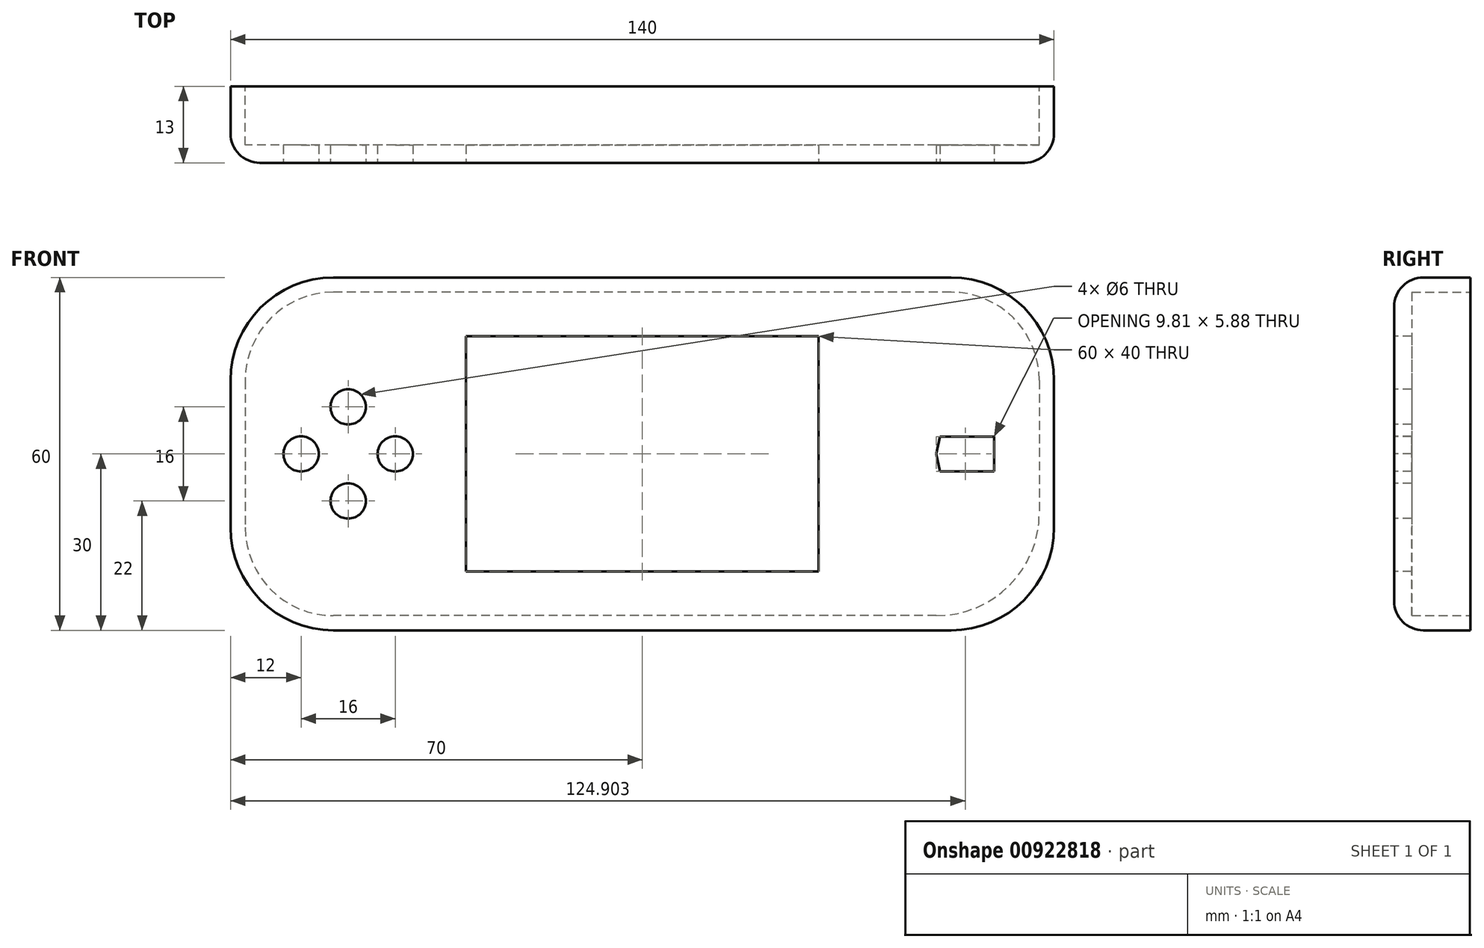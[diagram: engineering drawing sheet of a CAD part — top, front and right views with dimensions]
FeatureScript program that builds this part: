
annotation { "Feature Type Name" : "Feature", "Feature Type Description" : "" }
export const myFeature = defineFeature(function(context is Context, id is Id, definition is map)
    precondition{}
    {
        {
            var Q0;
            Q0=qCreatedBy(makeId("Front.planeOp"),FACE);
            var sketch = newSketch(context, id + "F0", { "sketchPlane" : qUnion([Q0])});
            skLineSegment(sketch, "E0.bottom", {"start": v(-70, 30) * mm, "end": v(70, 30) * mm});
            skLineSegment(sketch, "E0.top", {"start": v(-70, -30) * mm, "end": v(70, -30) * mm});
            skLineSegment(sketch, "E0.left", {"start": v(-70, 30) * mm, "end": v(-70, -30) * mm});
            skLineSegment(sketch, "E0.right", {"start": v(70, 30) * mm, "end": v(70, -30) * mm});
            skPoint(sketch, "E0.middle", {"position": v(0, 0) * mm});
            skSolve(sketch);
        }
        {
            var Q0;
            Q0 = qSketchRegion(id + "F0", true);
            extrude(context, id + "F1", {"entities" : qUnion([Q0]), "depth" : 13 * mm, "offsetDistance" : 25 * mm});
        }
        {
            var Q0;
            Q0=makeQuery(id+"F1.opExtrude","CAP_FACE",FACE,{"disambiguationData":[OSD([sQuery(id+"F0.wireOp",EDGE,"E0.bottom"),sQuery(id+"F0.wireOp",EDGE,"E0.top"),sQuery(id+"F0.wireOp",EDGE,"E0.left"),sQuery(id+"F0.wireOp",EDGE,"E0.right")])],"isStart":false});
            fillet(context, id + "F2", {"entities" : qUnion([Q0]), "radius" : 5 * mm, "tangentPropagation" : true, "allowEdgeOverflow" : false});
        }
        {
            var Q0;
            Q0=makeQuery(id+"F1.opExtrude","SWEPT_EDGE",EDGE,{"disambiguationData":[OSD([sQuery(id+"F0.wireOp",EDGE,"E0.bottom"),sQuery(id+"F0.wireOp",EDGE,"E0.left")])]});
            var Q1;
            Q1=makeQuery(id+"F1.opExtrude","SWEPT_EDGE",EDGE,{"disambiguationData":[OSD([sQuery(id+"F0.wireOp",EDGE,"E0.top"),sQuery(id+"F0.wireOp",EDGE,"E0.left")])]});
            var Q2;
            Q2=makeQuery(id+"F2.opFillet","BLEND_EDGE",EDGE,{"blendedFrom":[makeQuery(id+"F1.opExtrude","CAP_EDGE",EDGE,{"disambiguationData":[OSD([sQuery(id+"F0.wireOp",EDGE,"E0.bottom")])],"isStart":false}),makeQuery(id+"F1.opExtrude","CAP_EDGE",EDGE,{"disambiguationData":[OSD([sQuery(id+"F0.wireOp",EDGE,"E0.right")])],"isStart":false})],"blendedInto":[]});
            var Q3;
            Q3=makeQuery(id+"F2.opFillet","BLEND_EDGE",EDGE,{"blendedFrom":[makeQuery(id+"F1.opExtrude","CAP_EDGE",EDGE,{"disambiguationData":[OSD([sQuery(id+"F0.wireOp",EDGE,"E0.top")])],"isStart":false}),makeQuery(id+"F1.opExtrude","CAP_EDGE",EDGE,{"disambiguationData":[OSD([sQuery(id+"F0.wireOp",EDGE,"E0.right")])],"isStart":false})],"blendedInto":[]});
            fillet(context, id + "F3", {"entities" : qUnion([Q0, Q1, Q2, Q3]), "radius" : 17.5 * mm, "tangentPropagation" : true, "allowEdgeOverflow" : false});
        }
        {
            var Q0;
            Q0=makeQuery(id+"F1.opExtrude","CAP_FACE",FACE,{"disambiguationData":[OSD([sQuery(id+"F0.wireOp",EDGE,"E0.bottom"),sQuery(id+"F0.wireOp",EDGE,"E0.top"),sQuery(id+"F0.wireOp",EDGE,"E0.left"),sQuery(id+"F0.wireOp",EDGE,"E0.right")])],"isStart":false});
            var sketch = newSketch(context, id + "F4", { "sketchPlane" : qUnion([Q0])});
            skLineSegment(sketch, "E1", {"start": v(0, 0) * mm, "end": v(-50, 0) * mm});
            skLineSegment(sketch, "E2", {"start": v(0, 0) * mm, "end": v(50, 0) * mm});
            skLineSegment(sketch, "E3", {"start": v(-50, 0) * mm, "end": v(-50, 8) * mm});
            skLineSegment(sketch, "E4", {"start": v(-50, 0) * mm, "end": v(-42, 0) * mm});
            skLineSegment(sketch, "E5", {"start": v(-50, 0) * mm, "end": v(-50, -8) * mm});
            skLineSegment(sketch, "E6", {"start": v(-50, 0) * mm, "end": v(-58, 0) * mm});
            skLineSegment(sketch, "E7", {"start": v(50, 0) * mm, "end": v(52.5, 12.5) * mm});
            skLineSegment(sketch, "E8", {"start": v(52.5, 12.5) * mm, "end": v(50, 0) * mm});
            skLineSegment(sketch, "E9", {"start": v(50, 0) * mm, "end": v(52.5, -12.5) * mm});
            skLineSegment(sketch, "E10", {"start": v(52.5, -12.5) * mm, "end": v(50, 0) * mm});
            skLineSegment(sketch, "E11", {"start": v(50, 0) * mm, "end": v(59.8, 1.96) * mm});
            skLineSegment(sketch, "E12", {"start": v(50, 0) * mm, "end": v(40, 0) * mm});
            skCircle(sketch, "E13", {"center": v(-50, 8) * mm, "radius": 3 * mm});
            skCircle(sketch, "E14", {"center": v(-58, 0) * mm, "radius": 3 * mm});
            skCircle(sketch, "E15", {"center": v(-42, 0) * mm, "radius": 3 * mm});
            skCircle(sketch, "E16", {"center": v(-50, -8) * mm, "radius": 3 * mm});
            skLineSegment(sketch, "E17", {"start": v(50, 0) * mm, "end": v(47, 0) * mm});
            skLineSegment(sketch, "E18", {"start": v(50, 0) * mm, "end": v(50.59, 2.94) * mm});
            skLineSegment(sketch, "E19", {"start": v(50, 0) * mm, "end": v(52.94, 0.59) * mm});
            skLineSegment(sketch, "E20", {"start": v(50, 0) * mm, "end": v(50.59, -2.94) * mm});
            skLineSegment(sketch, "E21.bottom", {"start": v(47, 2.94) * mm, "end": v(52.94, 2.94) * mm});
            skLineSegment(sketch, "E21.top", {"start": v(47, 12.5) * mm, "end": v(52.94, 12.5) * mm});
            skLineSegment(sketch, "E21.left", {"start": v(47, 2.94) * mm, "end": v(47, 12.5) * mm});
            skLineSegment(sketch, "E21.right", {"start": v(52.94, 2.94) * mm, "end": v(52.94, 12.5) * mm});
            skLineSegment(sketch, "E22.bottom", {"start": v(47, 2.94) * mm, "end": v(40, 2.94) * mm});
            skLineSegment(sketch, "E22.top", {"start": v(47, -2.94) * mm, "end": v(40, -2.94) * mm});
            skLineSegment(sketch, "E22.left", {"start": v(47, 2.94) * mm, "end": v(47, -2.94) * mm});
            skLineSegment(sketch, "E22.right", {"start": v(40, 2.94) * mm, "end": v(40, -2.94) * mm});
            skLineSegment(sketch, "E23.bottom", {"start": v(47, -2.94) * mm, "end": v(52.94, -2.94) * mm});
            skLineSegment(sketch, "E23.top", {"start": v(47, -12.5) * mm, "end": v(52.94, -12.5) * mm});
            skLineSegment(sketch, "E23.left", {"start": v(47, -2.94) * mm, "end": v(47, -12.5) * mm});
            skLineSegment(sketch, "E23.right", {"start": v(52.94, -2.94) * mm, "end": v(52.94, -12.5) * mm});
            skLineSegment(sketch, "E24.bottom", {"start": v(52.94, -2.94) * mm, "end": v(59.8, -2.94) * mm});
            skLineSegment(sketch, "E24.top", {"start": v(52.94, 2.94) * mm, "end": v(59.8, 2.94) * mm});
            skLineSegment(sketch, "E24.left", {"start": v(52.94, -2.94) * mm, "end": v(52.94, 2.94) * mm});
            skLineSegment(sketch, "E24.right", {"start": v(59.8, -2.94) * mm, "end": v(59.8, 2.94) * mm});
            skSolve(sketch);
        }
        {
            var Q0;
            Q0=makeQuery(id+"F4.imprint","IMPRINT",FACE,{"disambiguationData":[TD([[makeQuery(id+"F4.imprint","IMPRINT",EDGE,{"derivedFrom":sQuery(id+"F4.wireOp",EDGE,"E16")}),1.0]])]});
            var Q1;
            {var subQ0=sQuery(id+"F4.wireOp",EDGE,"E4");var subQ1=sQuery(id+"F4.wireOp",EDGE,"E1");var subQ2=makeQuery(id+"F4.imprint","INTERSECT",VERTEX,{"derivedFrom":[subQ1,subQ0]});Q1=makeQuery(id+"F4.imprint","IMPRINT",FACE,{"disambiguationData":[TD([[makeQuery(id+"F4.imprint","IMPRINT",EDGE,{"disambiguationData":[TD([[subQ2,1.0]])],"derivedFrom":subQ1}),1.0]])]});}
            var Q2;
            {var subQ0=sQuery(id+"F4.wireOp",EDGE,"E4");var subQ1=sQuery(id+"F4.wireOp",EDGE,"E1");var subQ2=makeQuery(id+"F4.imprint","INTERSECT",VERTEX,{"derivedFrom":[subQ1,subQ0]});Q2=makeQuery(id+"F4.imprint","IMPRINT",FACE,{"disambiguationData":[TD([[makeQuery(id+"F4.imprint","IMPRINT",EDGE,{"disambiguationData":[TD([[subQ2,1.0]])],"derivedFrom":subQ1}),-1.0]])]});}
            var Q3;
            Q3=makeQuery(id+"F4.imprint","IMPRINT",FACE,{"disambiguationData":[TD([[makeQuery(id+"F4.imprint","IMPRINT",EDGE,{"derivedFrom":sQuery(id+"F4.wireOp",EDGE,"E14")}),1.0]])]});
            var Q4;
            Q4=makeQuery(id+"F4.imprint","IMPRINT",FACE,{"disambiguationData":[TD([[makeQuery(id+"F4.imprint","IMPRINT",EDGE,{"derivedFrom":sQuery(id+"F4.wireOp",EDGE,"E13")}),1.0]])]});
            var Q5;
            {var subQ0=sQuery(id+"F4.wireOp",EDGE,"E8");Q5=makeQuery(id+"F4.imprint","IMPRINT",FACE,{"disambiguationData":[TD([[makeQuery(id+"F4.imprint","IMPRINT",EDGE,{"derivedFrom":subQ0}),-1.0]])]});}
            var Q6;
            {var subQ0=sQuery(id+"F4.wireOp",EDGE,"E8");Q6=makeQuery(id+"F4.imprint","IMPRINT",FACE,{"disambiguationData":[TD([[makeQuery(id+"F4.imprint","IMPRINT",EDGE,{"derivedFrom":subQ0}),1.0]])]});}
            var Q7;
            {var subQ0=sQuery(id+"F4.wireOp",EDGE,"E18");Q7=makeQuery(id+"F4.imprint","IMPRINT",FACE,{"disambiguationData":[TD([[makeQuery(id+"F4.imprint","IMPRINT",EDGE,{"derivedFrom":subQ0}),-1.0]])]});}
            var Q8;
            {var subQ0=sQuery(id+"F4.wireOp",EDGE,"E17");Q8=makeQuery(id+"F4.imprint","IMPRINT",FACE,{"disambiguationData":[TD([[makeQuery(id+"F4.imprint","IMPRINT",EDGE,{"derivedFrom":subQ0}),-1.0]])]});}
            var Q9;
            {var subQ0=sQuery(id+"F4.wireOp",EDGE,"E17");Q9=makeQuery(id+"F4.imprint","IMPRINT",FACE,{"disambiguationData":[TD([[makeQuery(id+"F4.imprint","IMPRINT",EDGE,{"derivedFrom":subQ0}),1.0]])]});}
            var Q10;
            {var subQ0=sQuery(id+"F4.wireOp",EDGE,"E19");Q10=makeQuery(id+"F4.imprint","IMPRINT",FACE,{"disambiguationData":[TD([[makeQuery(id+"F4.imprint","IMPRINT",EDGE,{"derivedFrom":subQ0}),-1.0]])]});}
            var Q11;
            {var subQ0=sQuery(id+"F4.wireOp",EDGE,"E11");Q11=makeQuery(id+"F4.imprint","IMPRINT",FACE,{"disambiguationData":[TD([[makeQuery(id+"F4.imprint","IMPRINT",EDGE,{"derivedFrom":subQ0}),1.0]])]});}
            var Q12;
            {var subQ0=sQuery(id+"F4.wireOp",EDGE,"E11");Q12=makeQuery(id+"F4.imprint","IMPRINT",FACE,{"disambiguationData":[TD([[makeQuery(id+"F4.imprint","IMPRINT",EDGE,{"derivedFrom":subQ0}),-1.0]])]});}
            var Q13;
            {var subQ0=sQuery(id+"F4.wireOp",EDGE,"E12");Q13=makeQuery(id+"F4.imprint","IMPRINT",FACE,{"disambiguationData":[TD([[makeQuery(id+"F4.imprint","IMPRINT",EDGE,{"derivedFrom":subQ0}),-1.0]])]});}
            var Q14;
            {var subQ0=sQuery(id+"F4.wireOp",EDGE,"E12");Q14=makeQuery(id+"F4.imprint","IMPRINT",FACE,{"disambiguationData":[TD([[makeQuery(id+"F4.imprint","IMPRINT",EDGE,{"derivedFrom":subQ0}),1.0]])]});}
            var Q15;
            {var subQ0=sQuery(id+"F4.wireOp",EDGE,"E10");Q15=makeQuery(id+"F4.imprint","IMPRINT",FACE,{"disambiguationData":[TD([[makeQuery(id+"F4.imprint","IMPRINT",EDGE,{"derivedFrom":subQ0}),1.0]])]});}
            var Q16;
            {var subQ0=sQuery(id+"F4.wireOp",EDGE,"E10");Q16=makeQuery(id+"F4.imprint","IMPRINT",FACE,{"disambiguationData":[TD([[makeQuery(id+"F4.imprint","IMPRINT",EDGE,{"derivedFrom":subQ0}),-1.0]])]});}
            extrude(context, id + "F5", {"entities" : qUnion([Q0, Q1, Q2, Q3, Q4, Q5, Q6, Q7, Q8, Q9, Q10, Q11, Q12, Q13, Q14, Q15, Q16]), "operationType" : NewBodyOperationType.REMOVE, "oppositeDirection" : true, "depth" : 25 * mm, "offsetDistance" : 25 * mm});
        }
        {
            var Q0;
            Q0=makeQuery(id+"F1.opExtrude","CAP_FACE",FACE,{"disambiguationData":[OSD([sQuery(id+"F0.wireOp",EDGE,"E0.bottom"),sQuery(id+"F0.wireOp",EDGE,"E0.top"),sQuery(id+"F0.wireOp",EDGE,"E0.left"),sQuery(id+"F0.wireOp",EDGE,"E0.right")])],"isStart":false});
            var sketch = newSketch(context, id + "F6", { "sketchPlane" : qUnion([Q0])});
            skLineSegment(sketch, "E25.bottom", {"start": v(-30, 20) * mm, "end": v(30, 20) * mm});
            skLineSegment(sketch, "E25.top", {"start": v(-30, -20) * mm, "end": v(30, -20) * mm});
            skLineSegment(sketch, "E25.left", {"start": v(-30, 20) * mm, "end": v(-30, -20) * mm});
            skLineSegment(sketch, "E25.right", {"start": v(30, 20) * mm, "end": v(30, -20) * mm});
            skPoint(sketch, "E25.middle", {"position": v(0, 0) * mm});
            skSolve(sketch);
        }
        {
            var Q0;
            Q0=makeQuery(id+"F6.imprint","IMPRINT",FACE,{"disambiguationData":[TD([[makeQuery(id+"F6.imprint","IMPRINT",EDGE,{"derivedFrom":sQuery(id+"F6.wireOp",EDGE,"E25.bottom")}),-1.0]])]});
            extrude(context, id + "F7", {"entities" : qUnion([Q0]), "operationType" : NewBodyOperationType.REMOVE, "oppositeDirection" : true, "depth" : 25 * mm, "offsetDistance" : 25 * mm});
        }
        {
            var Q0;
            Q0=makeQuery(id+"F1.opExtrude","CAP_FACE",FACE,{"disambiguationData":[OSD([sQuery(id+"F0.wireOp",EDGE,"E0.bottom"),sQuery(id+"F0.wireOp",EDGE,"E0.top"),sQuery(id+"F0.wireOp",EDGE,"E0.left"),sQuery(id+"F0.wireOp",EDGE,"E0.right")])],"isStart":true});
            var sketch = newSketch(context, id + "F8", { "sketchPlane" : qUnion([Q0])});
            skLineSegment(sketch, "E26.bottom", {"start": v(-52.5, 27.5) * mm, "end": v(52.5, 27.5) * mm});
            skLineSegment(sketch, "E26.top", {"start": v(-50, -27.5) * mm, "end": v(52.5, -27.5) * mm});
            skLineSegment(sketch, "E26.left", {"start": v(-67.5, 12.5) * mm, "end": v(-67.5, -10) * mm});
            skLineSegment(sketch, "E26.right", {"start": v(67.5, 12.5) * mm, "end": v(67.5, -12.5) * mm});
            skPoint(sketch, "E26.middle", {"position": v(0, 0) * mm});
            skPoint(sketch, "E27.visualSharp", {"position": v(-67.5, -27.5) * mm});
            skArc(sketch, "E27.filletArc", {"start": v(-67.5, -10) * mm, "mid": v(-62.37, -22.37) * mm, "end": v(-50, -27.5) * mm});
            skPoint(sketch, "E28.visualSharp", {"position": v(-67.5, 27.5) * mm});
            skArc(sketch, "E28.filletArc", {"start": v(-52.5, 27.5) * mm, "mid": v(-63.1, 23.1) * mm, "end": v(-67.5, 12.5) * mm});
            skPoint(sketch, "E29.visualSharp", {"position": v(67.5, 27.5) * mm});
            skArc(sketch, "E29.filletArc", {"start": v(67.5, 12.5) * mm, "mid": v(63.1, 23.1) * mm, "end": v(52.5, 27.5) * mm});
            skPoint(sketch, "E30.visualSharp", {"position": v(67.5, -27.5) * mm});
            skArc(sketch, "E30.filletArc", {"start": v(52.5, -27.5) * mm, "mid": v(63.1, -23.1) * mm, "end": v(67.5, -12.5) * mm});
            skSolve(sketch);
        }
        {
            var Q0;
            Q0 = qSketchRegion(id + "F8", true);
            extrude(context, id + "F9", {"entities" : qUnion([Q0]), "operationType" : NewBodyOperationType.REMOVE, "oppositeDirection" : true, "depth" : 10 * mm, "offsetDistance" : 25 * mm});
        }
    });
